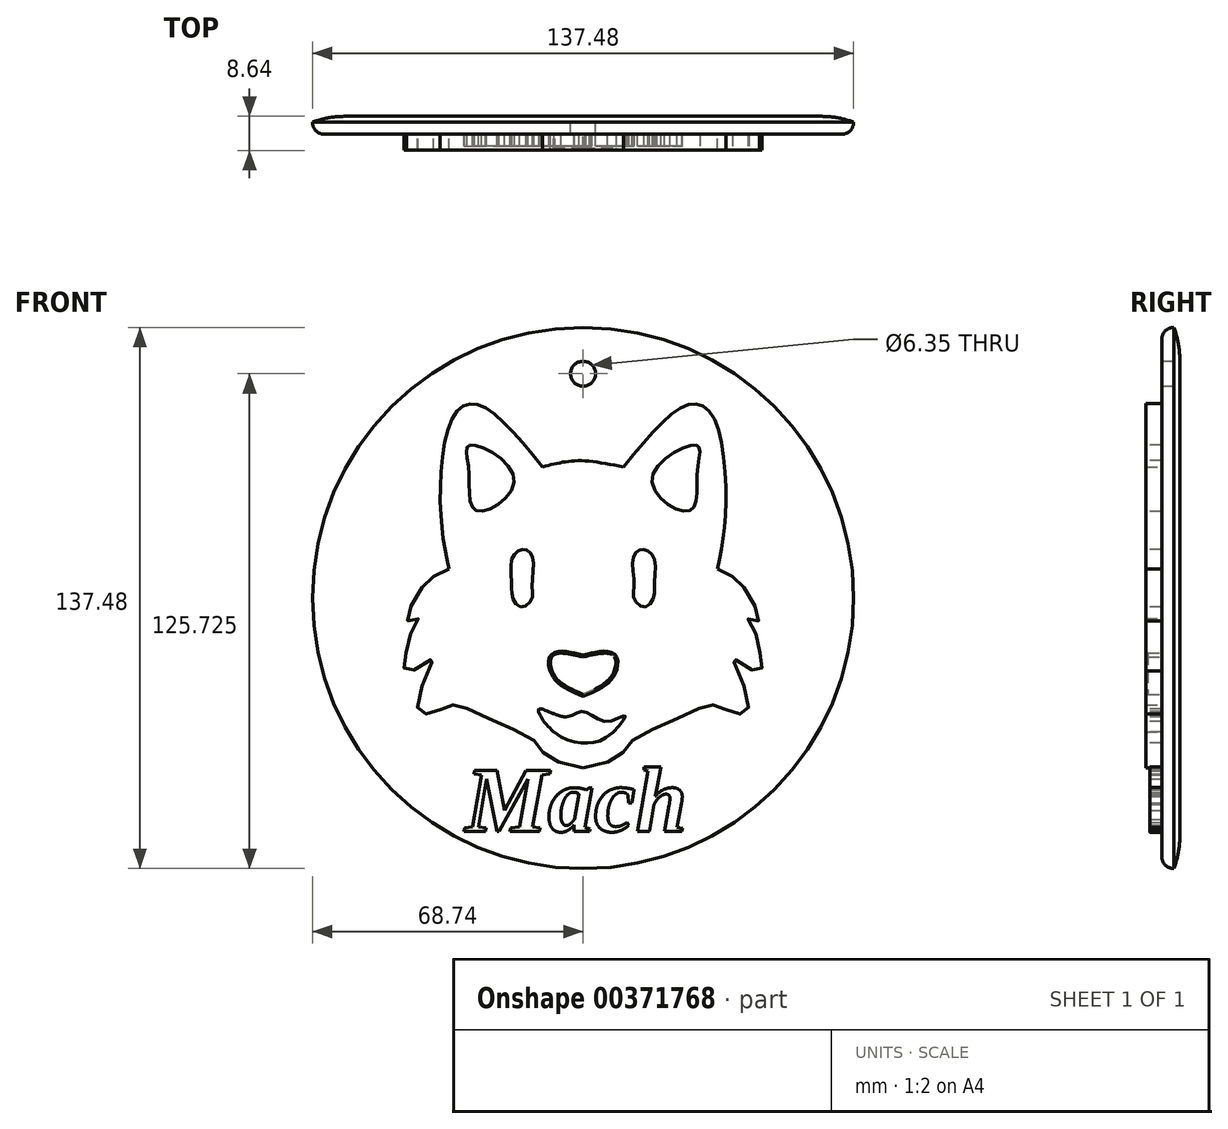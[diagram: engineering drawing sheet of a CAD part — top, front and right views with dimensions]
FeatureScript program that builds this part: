
annotation { "Feature Type Name" : "Feature", "Feature Type Description" : "" }
export const myFeature = defineFeature(function(context is Context, id is Id, definition is map)
    precondition{}
    {
        {
            var Q0;
            Q0=qCreatedBy(makeId("Front.planeOp"),FACE);
            var sketch = newSketch(context, id + "F0", { "sketchPlane" : qUnion([Q0])});
            skFitSpline(sketch, "E0", {"points": [v(-34.1, 7.32) * mm, v(-36.26, 23.6) * mm, v(-32.52, 46.91) * mm, v(-26.2, 48.93) * mm, v(-10.27, 33.33) * mm], "startDerivative": vector(-12.05, 57.47) * mm, "endDerivative": vector(58.28, -71.48) * mm});
            skFitSpline(sketch, "E1.MirrorCS", {"points": [v(34.1, 7.32) * mm, v(36.26, 23.6) * mm, v(32.52, 46.91) * mm, v(26.2, 48.93) * mm, v(10.27, 33.33) * mm], "startDerivative": vector(12.05, 57.47) * mm, "endDerivative": vector(-58.28, -71.48) * mm});
            skFitSpline(sketch, "E2", {"points": [v(-28.78, 38.85) * mm, v(-29.07, 32.8) * mm, v(-26.95, 22.14) * mm, v(-17.5, 30.17) * mm, v(-28.78, 38.85) * mm]});
            skFitSpline(sketch, "E3.MirrorC", {"points": [v(28.78, 38.85) * mm, v(29.07, 32.8) * mm, v(26.95, 22.14) * mm, v(17.5, 30.17) * mm, v(28.78, 38.85) * mm]});
            skFitSpline(sketch, "E4", {"points": [v(-34.1, 7.32) * mm, v(-38.85, 4.9) * mm, v(-42.6, 0) * mm, v(-44.6, -5.76) * mm, v(-42.02, -5.18) * mm, v(-44.03, -9.5) * mm, v(-45.19, -16.12) * mm, v(-45.19, -18.42) * mm, v(-40.3, -16.98) * mm, v(-38, -14.97) * mm, v(-41.44, -23.89) * mm, v(-41.44, -29.07) * mm, v(-38, -29.07) * mm, v(-34.1, -27.34) * mm, v(-31.37, -27.34) * mm, v(-22.45, -31.37) * mm, v(-12.09, -36.55) * mm, v(-9.5, -40) * mm, v(0, -43.17) * mm], "startDerivative": vector(-93.04, -38.04) * mm, "endDerivative": vector(153.7, -32.72) * mm});
            skFitSpline(sketch, "E5.MirrorCS", {"points": [v(34.1, 7.32) * mm, v(38.85, 4.9) * mm, v(42.6, 0) * mm, v(44.6, -5.76) * mm, v(42.02, -5.18) * mm, v(44.03, -9.5) * mm, v(45.19, -16.12) * mm, v(45.19, -18.42) * mm, v(40.3, -16.98) * mm, v(38, -14.97) * mm, v(41.44, -23.89) * mm, v(41.44, -29.07) * mm, v(38, -29.07) * mm, v(34.1, -27.34) * mm, v(31.37, -27.34) * mm, v(22.45, -31.37) * mm, v(12.09, -36.55) * mm, v(9.5, -40) * mm, v(0, -43.17) * mm], "startDerivative": vector(93.04, -38.04) * mm, "endDerivative": vector(-153.7, -32.72) * mm});
            skFitSpline(sketch, "E6", {"points": [v(-10.27, 33.33) * mm, v(-5.54, 34.43) * mm, v(0, 34.87) * mm, v(10.27, 33.33) * mm], "startDerivative": vector(16.61, 4.38) * mm, "endDerivative": vector(26.66, -5.09) * mm});
            skFitSpline(sketch, "E7", {"points": [v(0, -14.97) * mm, v(-7.77, -14.68) * mm, v(-7.2, -19.86) * mm, v(0, -24.46) * mm], "startDerivative": vector(-28.18, 6.66) * mm, "endDerivative": vector(23.28, -9.7) * mm});
            skFitSpline(sketch, "E8.MirrorCS", {"points": [v(0, -14.97) * mm, v(7.77, -14.68) * mm, v(7.2, -19.86) * mm, v(0, -24.46) * mm], "startDerivative": vector(28.18, 6.66) * mm, "endDerivative": vector(-23.28, -9.7) * mm});
            skFitSpline(sketch, "E9", {"points": [v(-18.13, 9.79) * mm, v(-18.13, 3.45) * mm, v(-17.84, 0) * mm, v(-15.54, -2.3) * mm, v(-12.95, 0) * mm, v(-12.95, 3.17) * mm, v(-12.66, 9.79) * mm, v(-14.1, 12.1) * mm, v(-16.12, 12.1) * mm, v(-18.13, 9.79) * mm]});
            skFitSpline(sketch, "E10.MirrorC", {"points": [v(18.13, 9.79) * mm, v(18.13, 3.45) * mm, v(17.84, 0) * mm, v(15.54, -2.3) * mm, v(12.95, 0) * mm, v(12.95, 3.17) * mm, v(12.66, 9.79) * mm, v(14.1, 12.1) * mm, v(16.12, 12.1) * mm, v(18.13, 9.79) * mm]});
            skFitSpline(sketch, "E11", {"points": [v(0, -28.78) * mm, v(-4.32, -30.22) * mm, v(-11.22, -28.2) * mm, v(-7.48, -33.96) * mm, v(0, -36.84) * mm, v(6.33, -35.11) * mm, v(10.65, -29.93) * mm, v(5.76, -31.37) * mm, v(0, -28.78) * mm]});
            skFitSpline(sketch, "E12", {"points": [v(-7.2, -29.52) * mm, v(-7.48, -29.4) * mm, v(-7.48, -33.96) * mm, v(-4.32, -30.22) * mm], "startDerivative": vector(-2.63, 2.83) * mm, "endDerivative": vector(8.7, 14.86) * mm});
            skSolve(sketch);
        }
        {
            var Q0;
            Q0=makeQuery(id+"F0.imprint","IMPRINT",FACE,{"disambiguationData":[TD([[makeQuery(id+"F0.imprint","IMPRINT",EDGE,{"derivedFrom":sQuery(id+"F0.wireOp",EDGE,"E0")}),-1.0]])]});
            extrude(context, id + "F1", {"entities" : qUnion([Q0]), "depth" : 8.64 * mm});
        }
        {
            var Q0;
            Q0=qCreatedBy(makeId("Front.planeOp"),FACE);
            var sketch = newSketch(context, id + "F2", { "sketchPlane" : qUnion([Q0])});
            skCircle(sketch, "E13", {"center": v(0, 0) * mm, "radius": 68.74 * mm});
            skSolve(sketch);
        }
        {
            var Q0;
            Q0=makeQuery(id+"F2.imprint","IMPRINT",FACE,{"disambiguationData":[TD([[makeQuery(id+"F2.imprint","IMPRINT",EDGE,{"derivedFrom":sQuery(id+"F2.wireOp",EDGE,"E13")}),1.0]])]});
            extrude(context, id + "F3", {"entities" : qUnion([Q0]), "operationType" : NewBodyOperationType.ADD, "depth" : 4.57 * mm});
        }
        {
            var Q0;
            Q0=qCreatedBy(makeId("Front.planeOp"),FACE);
            var sketch = newSketch(context, id + "F4", { "sketchPlane" : qUnion([Q0])});
            skText(sketch, "E14", { "text": "Mach", "fontName": "Tinos-BoldItalic.ttf"});
            const initialGuessF4  = {"E14": [-0.02993, -0.05929, 1, 0, 0.01698]};
            skSetInitialGuess(sketch, initialGuessF4);
            skSolve(sketch);
        }
        {
            var Q0;
            Q0 = qSketchRegion(id + "F4", true);
            extrude(context, id + "F5", {"entities" : qUnion([Q0]), "operationType" : NewBodyOperationType.ADD, "depth" : 7.62 * mm});
        }
        {
            var Q0;
            Q0=makeQuery(id+"F3.opExtrude","CAP_EDGE",EDGE,{"disambiguationData":[OSD([sQuery(id+"F2.wireOp",EDGE,"E13")])],"isStart":false});
            fillet(context, id + "F6", {"entities" : qUnion([Q0]), "radius" : 3.07 * mm, "tangentPropagation" : true, "allowEdgeOverflow" : false});
        }
        {
            var Q0;
            Q0=makeQuery(id+"F3.opExtrude","CAP_EDGE",EDGE,{"disambiguationData":[OSD([sQuery(id+"F2.wireOp",EDGE,"E13")])],"isStart":true});
            fillet(context, id + "F7", {"entities" : qUnion([Q0]), "radius" : 22.08 * mm, "tangentPropagation" : true, "allowEdgeOverflow" : false});
        }
        {
            var Q0;
            Q0=qCreatedBy(makeId("Front.planeOp"),FACE);
            var sketch = newSketch(context, id + "F8", { "sketchPlane" : qUnion([Q0])});
            skCircle(sketch, "E15", {"center": v(0, 56.99) * mm, "radius": 4.9 * mm});
            skSolve(sketch);
        }
        {
            var Q0;
            Q0=sQuery(id+"F8.wireOp",VERTEX,"E15.center");
            var Q1;
            Q1=makeQuery(id+"F1.opExtrude","SWEPT_BODY",BODY,{"disambiguationData":[OSD([sQuery(id+"F0.wireOp",EDGE,"E0"),sQuery(id+"F0.wireOp",EDGE,"E1.MirrorCS"),sQuery(id+"F0.wireOp",EDGE,"E2"),sQuery(id+"F0.wireOp",EDGE,"E3.MirrorC"),sQuery(id+"F0.wireOp",EDGE,"E4"),sQuery(id+"F0.wireOp",EDGE,"E5.MirrorCS"),sQuery(id+"F0.wireOp",EDGE,"E6"),sQuery(id+"F0.wireOp",EDGE,"E7"),sQuery(id+"F0.wireOp",EDGE,"E8.MirrorCS"),sQuery(id+"F0.wireOp",EDGE,"E9"),sQuery(id+"F0.wireOp",EDGE,"E10.MirrorC")])]});
            hole(context, id + "F9", {"style" : HoleStyle.SIMPLE, "endStyle" : HoleEndStyle.THROUGH, "oppositeDirection" : true, "holeDiameter" : 6.35 * mm, "isTappedThrough" : true, "tappedDepth" : 12.7 * mm, "tapClearance" : 3, "locations" : qUnion([Q0]), "scope" : qUnion([Q1])});
        }
        {
            var Q0;
            Q0=makeQuery(id+"F1.opExtrude","CAP_EDGE",EDGE,{"disambiguationData":[OSD([sQuery(id+"F0.wireOp",EDGE,"E7")])],"isStart":false});
            var Q1;
            Q1=makeQuery(id+"F1.opExtrude","CAP_EDGE",EDGE,{"disambiguationData":[OSD([sQuery(id+"F0.wireOp",EDGE,"E8.MirrorCS")])],"isStart":false});
            chamfer(context, id + "F10", {"entities" : qUnion([Q0, Q1]), "width" : 0.5 * mm, "tangentPropagation" : true});
        }
    });
